# Revit family: Faucet-Two_Handle-American_Standard-Fluent-7186_Series
name_source: partatom
category: Plumbing Fixtures
revit_build: Autodesk Revit 2014 (Build: 20130308_1515(x64)
units: mm (PartAtom-declared; Revit-internal decimal feet)

## types (2) — shared parameters
ADA Compliant = Yes
Assembly Code = D2020300
CW Connection = Yes
CWFU = 1.5
Cold Water Connection Diameter = 1/2"
Default Elevation = 0"
Finish = Metal-American Standard-002-Polished Chrome
Flow Rate = 1.2 GPM (4.5 L/min)
HW Connection = Yes
HWFU = 1.5
Height = 6 7/8"
Hot Water Connection Diameter = 1/2"
Installation Type = Deck Mounted
Length = 7"
Manufacturer = American Standard
Material = Metal-American Standard-002-Polished Chrome
Price = Prices may vary. Please consult Manufacturer Representative for most up-to-date price list.
Product Documentation Link = https://www.americanstandard-us.com
Product Page URL = https://www.americanstandard-us.com
Specification = Two-handle widespread lavatory faucet shall feature cast brass valve bodies with flexible hose connections for 6" to 12"
installations. Shall also feature 1/4 turn washerless ceramic disc valve cartridges. Shall also feature a metal drain body with
stainless steel cable actuation.
URL = http://www.americanstandard-us.com
Vent Connection = No
Waste Connection = No
Width = 13 1/2"
zero-valued in all types: WFU

## per-type parameters (varying)
| type | Description | Indicators |
| 7186.801 | Metal Speed Connect® pop-up drain. Metal lever handles. | No |
| 7186.811 | Metal Speed Connect® pop-up drain. Metal lever handle with red and blue indicators. | Yes |

note: column(s) folded — value = type name in every type: Model

## geometry (parser evidence)
native form markers: Sweep x1
no freeform markers — native parametric forms only
